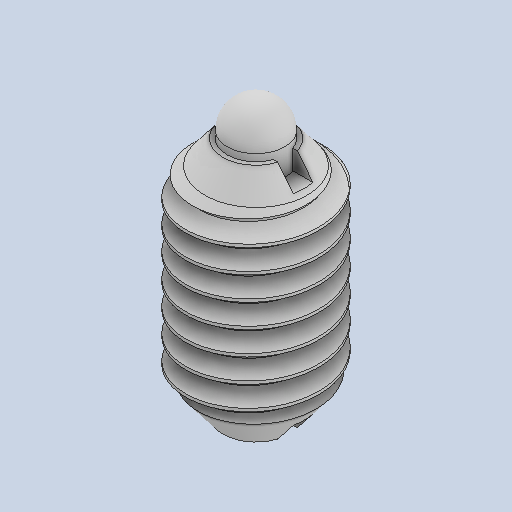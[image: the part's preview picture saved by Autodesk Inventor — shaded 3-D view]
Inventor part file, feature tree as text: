
AUTODESK INVENTOR PART (.ipt)
format: ipt  version: 2025 (Build 290162000, 162)  size: 443,904 bytes
history: native  units: in
note: dims shown in document units (in); Inventor stores cm internally (conversion verified against a paired STEP export)
features: revolve x1, other x1
ambient origin geometry x8: Origin, YZ Plane, XZ Plane, XY Plane, X Axis, Y Axis, Z Axis, Center Point
bodies: Solid1 (feature_tree), Solid2 (feature_tree)
feature tree (2):
  revolve  "Revolve2"  [1 undecoded]
  other  "Cut-Extrude14"
note: 1 required parameter value undecoded (feature->parameter linkage not recoverable at this tier; creation-order binding heuristic only, values carry confidence <= 0.55)
